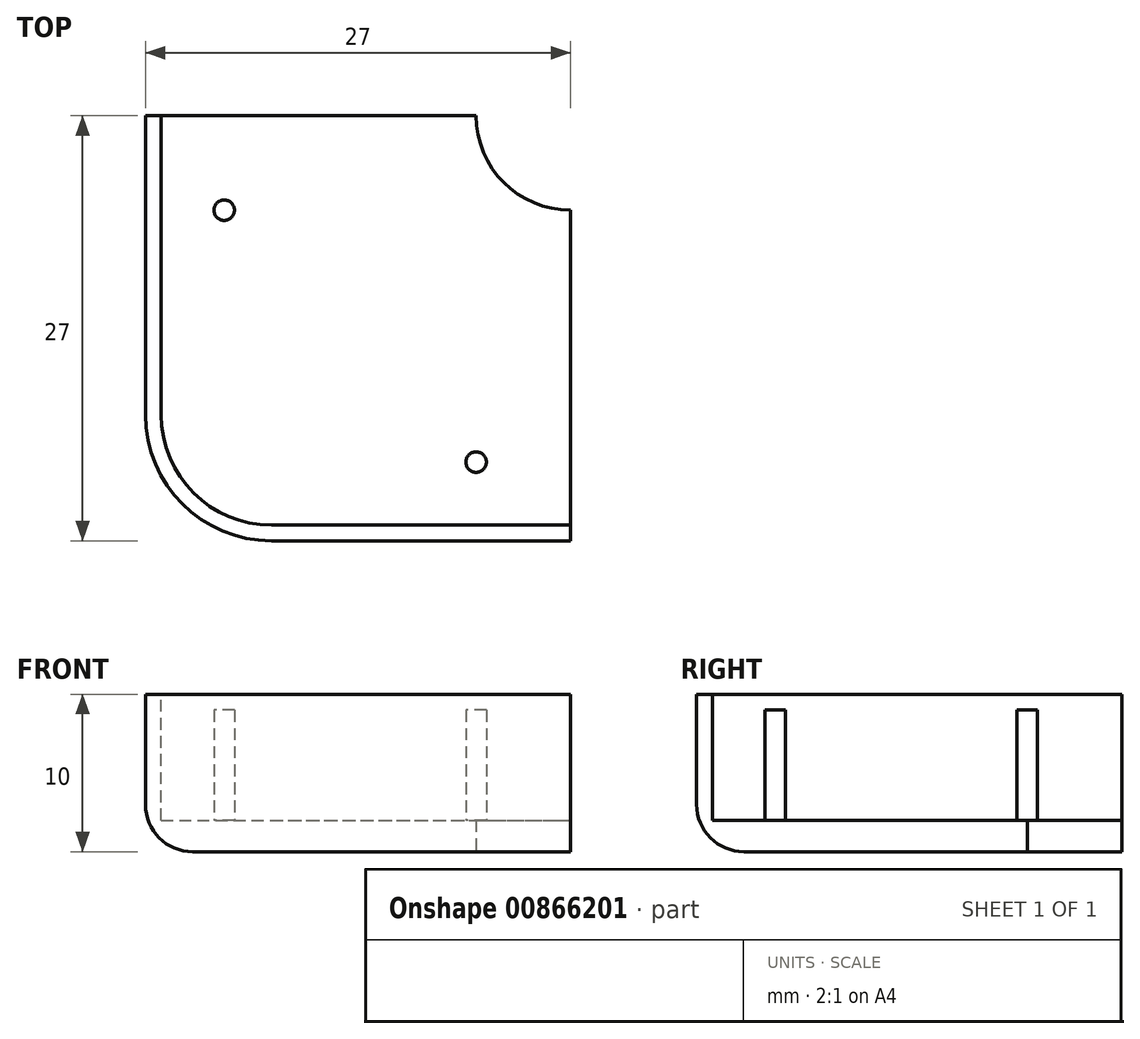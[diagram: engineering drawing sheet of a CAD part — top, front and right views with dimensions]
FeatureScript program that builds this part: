
annotation { "Feature Type Name" : "Feature", "Feature Type Description" : "" }
export const myFeature = defineFeature(function(context is Context, id is Id, definition is map)
    precondition{}
    {
        {
            var Q0;
            Q0=qCreatedBy(makeId("Top.planeOp"),FACE);
            var sketch = newSketch(context, id + "F0", { "sketchPlane" : qUnion([Q0])});
            skLineSegment(sketch, "E0.bottom", {"start": v(8, 0) * mm, "end": v(27, 0) * mm});
            skLineSegment(sketch, "E0.top", {"start": v(0, 27) * mm, "end": v(27, 27) * mm});
            skLineSegment(sketch, "E0.left", {"start": v(0, 8) * mm, "end": v(0, 27) * mm});
            skLineSegment(sketch, "E0.right", {"start": v(27, 0) * mm, "end": v(27, 21) * mm});
            skLineSegment(sketch, "E1", {"start": v(21, 27) * mm, "end": v(21, 27) * mm});
            skLineSegment(sketch, "E2", {"start": v(27, 21) * mm, "end": v(27, 21) * mm});
            skPoint(sketch, "E3.visualSharp", {"position": v(21, 21) * mm});
            skArc(sketch, "E3.filletArc", {"start": v(21, 27) * mm, "mid": v(22.76, 22.76) * mm, "end": v(27, 21) * mm});
            skPoint(sketch, "E4.visualSharp", {"position": v(0, 0) * mm});
            skArc(sketch, "E4.filletArc", {"start": v(0, 8) * mm, "mid": v(2.34, 2.34) * mm, "end": v(8, 0) * mm});
            skSolve(sketch);
        }
        {
            var Q0;
            Q0=makeQuery(id+"F0.imprint","IMPRINT",FACE,{"disambiguationData":[TD([[makeQuery(id+"F0.imprint","IMPRINT",EDGE,{"derivedFrom":sQuery(id+"F0.wireOp",EDGE,"E0.bottom")}),1.0]])]});
            extrude(context, id + "F1", {"entities" : qUnion([Q0]), "depth" : 10 * mm, "offsetDistance" : 25 * mm});
        }
        {
            var Q0;
            Q0=makeQuery(id+"F1.opExtrude","CAP_EDGE",EDGE,{"disambiguationData":[OSD([sQuery(id+"F0.wireOp",EDGE,"E0.bottom")])],"isStart":true});
            var Q1;
            Q1=makeQuery(id+"F1.opExtrude","CAP_EDGE",EDGE,{"disambiguationData":[OSD([sQuery(id+"F0.wireOp",EDGE,"E4.filletArc")])],"isStart":true});
            var Q2;
            Q2=makeQuery(id+"F1.opExtrude","CAP_EDGE",EDGE,{"disambiguationData":[OSD([sQuery(id+"F0.wireOp",EDGE,"E0.left")])],"isStart":true});
            fillet(context, id + "F2", {"entities" : qUnion([Q0, Q1, Q2]), "radius" : 3 * mm, "tangentPropagation" : true, "allowEdgeOverflow" : false});
        }
        {
            var Q0;
            Q0=makeQuery(id+"F1.opExtrude","CAP_FACE",FACE,{"disambiguationData":[OSD([sQuery(id+"F0.wireOp",EDGE,"E0.bottom"),sQuery(id+"F0.wireOp",EDGE,"E0.top"),sQuery(id+"F0.wireOp",EDGE,"E0.left"),sQuery(id+"F0.wireOp",EDGE,"E0.right"),sQuery(id+"F0.wireOp",EDGE,"E3.filletArc"),sQuery(id+"F0.wireOp",EDGE,"E4.filletArc")])],"isStart":false});
            var sketch = newSketch(context, id + "F3", { "sketchPlane" : qUnion([Q0])});
            skLineSegment(sketch, "E5.0", {"start": v(1, 26) * mm, "end": v(1, 8) * mm});
            skLineSegment(sketch, "E5.1", {"start": v(20.07, 26) * mm, "end": v(1, 26) * mm});
            skLineSegment(sketch, "E5.2", {"start": v(8, 1) * mm, "end": v(26, 1) * mm});
            skLineSegment(sketch, "E5.3", {"start": v(26, 1) * mm, "end": v(26, 20.07) * mm});
            skArc(sketch, "E5.4", {"start": v(26, 20.07) * mm, "mid": v(22.05, 22.05) * mm, "end": v(20.07, 26) * mm});
            skPoint(sketch, "E6.visualSharp", {"position": v(1, 1) * mm});
            skArc(sketch, "E6.filletArc", {"start": v(1, 8) * mm, "mid": v(3.05, 3.05) * mm, "end": v(8, 1) * mm});
            skLineSegment(sketch, "E7", {"start": v(1, 26) * mm, "end": v(1, 27) * mm});
            skLineSegment(sketch, "E8", {"start": v(26, 1) * mm, "end": v(27, 1) * mm});
            skSolve(sketch);
        }
        {
            var Q0;
            Q0=makeQuery(id+"F3.imprint","IMPRINT",FACE,{"disambiguationData":[TD([[makeQuery(id+"F3.imprint","IMPRINT",EDGE,{"derivedFrom":sQuery(id+"F3.wireOp",EDGE,"E5.0")}),1.0]])]});
            var Q1;
            Q1=makeQuery(id+"F3.imprint","IMPRINT",FACE,{"disambiguationData":[TD([[makeQuery(id+"F3.imprint","IMPRINT",EDGE,{"derivedFrom":sQuery(id+"F3.wireOp",EDGE,"E5.1")}),-1.0]])]});
            extrude(context, id + "F4", {"entities" : qUnion([Q0, Q1]), "operationType" : NewBodyOperationType.REMOVE, "oppositeDirection" : true, "depth" : 8 * mm, "offsetDistance" : 25 * mm});
        }
        {
            var Q0;
            Q0=makeQuery(id+"F4.boolean.opBoolean","COPY",FACE,{"derivedFrom":makeQuery(id+"F4.opExtrude","CAP_FACE",FACE,{"disambiguationData":[OSD([sQuery(id+"F0.wireOp",EDGE,"E0.top"),sQuery(id+"F0.wireOp",EDGE,"E0.right"),sQuery(id+"F0.wireOp",EDGE,"E3.filletArc"),sQuery(id+"F3.wireOp",EDGE,"E5.0"),sQuery(id+"F3.wireOp",EDGE,"E5.2"),sQuery(id+"F3.wireOp",EDGE,"E6.filletArc"),sQuery(id+"F3.wireOp",EDGE,"E7"),sQuery(id+"F3.wireOp",EDGE,"E8")])],"isStart":false})});
            var sketch = newSketch(context, id + "F5", { "sketchPlane" : qUnion([Q0])});
            skLineSegment(sketch, "E9", {"start": v(27, 27) * mm, "end": v(27, 5) * mm});
            skLineSegment(sketch, "E10", {"start": v(27, 27) * mm, "end": v(5, 27) * mm});
            skLineSegment(sketch, "E11", {"start": v(27, 5) * mm, "end": v(21, 5) * mm});
            skLineSegment(sketch, "E12", {"start": v(5, 27) * mm, "end": v(5, 21) * mm});
            skCircle(sketch, "E13", {"center": v(5, 21) * mm, "radius": 0.65 * mm});
            skCircle(sketch, "E14", {"center": v(21, 5) * mm, "radius": 0.65 * mm});
            skSolve(sketch);
        }
        {
            var Q0;
            Q0=makeQuery(id+"F5.imprint","IMPRINT",FACE,{"disambiguationData":[TD([[makeQuery(id+"F5.imprint","IMPRINT",EDGE,{"derivedFrom":sQuery(id+"F5.wireOp",EDGE,"E14")}),1.0]])]});
            var Q1;
            Q1=makeQuery(id+"F5.imprint","IMPRINT",FACE,{"disambiguationData":[TD([[makeQuery(id+"F5.imprint","IMPRINT",EDGE,{"derivedFrom":sQuery(id+"F5.wireOp",EDGE,"E13")}),1.0]])]});
            extrude(context, id + "F6", {"entities" : qUnion([Q0, Q1]), "operationType" : NewBodyOperationType.ADD, "depth" : 7 * mm, "offsetDistance" : 25 * mm});
        }
    });
